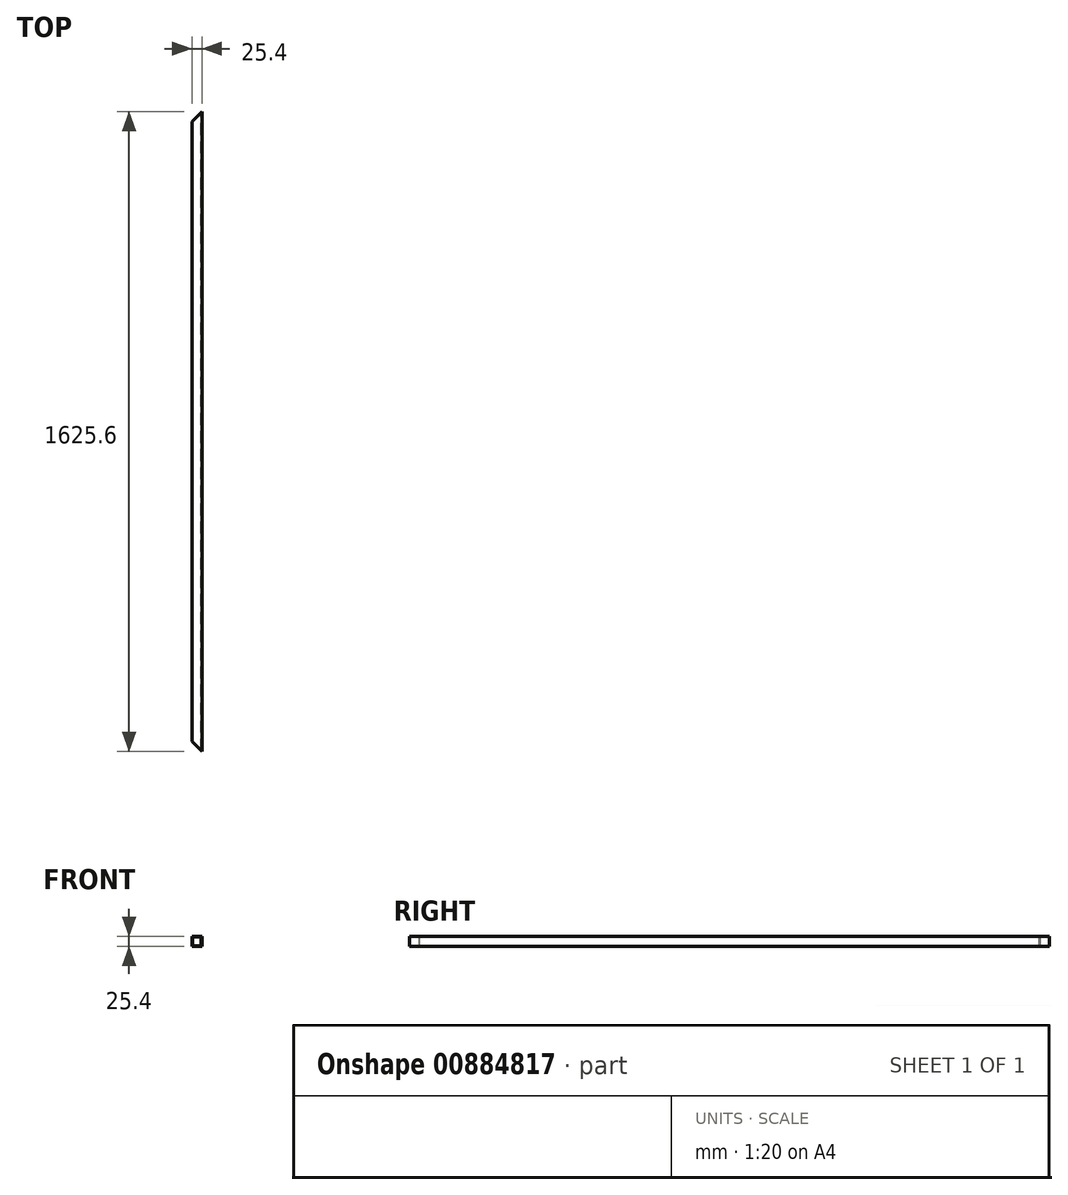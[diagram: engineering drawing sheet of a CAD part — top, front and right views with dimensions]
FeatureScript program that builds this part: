
annotation { "Feature Type Name" : "Feature", "Feature Type Description" : "" }
export const myFeature = defineFeature(function(context is Context, id is Id, definition is map)
    precondition{}
    {
        {
            var Q0;
            Q0=qCreatedBy(makeId("Front.planeOp"),FACE);
            var sketch = newSketch(context, id + "F0", { "sketchPlane" : qUnion([Q0])});
            skLineSegment(sketch, "E0.bottom", {"start": v(0, 0) * mm, "end": v(25.4, 0) * mm});
            skLineSegment(sketch, "E0.top", {"start": v(0, 25.4) * mm, "end": v(25.4, 25.4) * mm});
            skLineSegment(sketch, "E0.left", {"start": v(0, 0) * mm, "end": v(0, 25.4) * mm});
            skLineSegment(sketch, "E0.right", {"start": v(25.4, 0) * mm, "end": v(25.4, 25.4) * mm});
            skLineSegment(sketch, "E1.0", {"start": v(1.65, 1.65) * mm, "end": v(23.75, 1.65) * mm});
            skLineSegment(sketch, "E1.1", {"start": v(1.65, 1.65) * mm, "end": v(1.65, 23.75) * mm});
            skLineSegment(sketch, "E1.2", {"start": v(1.65, 23.75) * mm, "end": v(23.75, 23.75) * mm});
            skLineSegment(sketch, "E1.3", {"start": v(23.75, 1.65) * mm, "end": v(23.75, 23.75) * mm});
            skSolve(sketch);
        }
        {
            var Q0;
            Q0=makeQuery(id+"F0.imprint","IMPRINT",FACE,{"disambiguationData":[TD([[makeQuery(id+"F0.imprint","IMPRINT",EDGE,{"derivedFrom":sQuery(id+"F0.wireOp",EDGE,"E0.bottom")}),1.0]])]});
            extrude(context, id + "F1", {"entities" : qUnion([Q0]), "depth" : 1625.6 * mm, "offsetDistance" : 25.4 * mm});
        }
        {
            var Q0;
            Q0=makeQuery(id+"F1.opExtrude","SWEPT_FACE",FACE,{"disambiguationData":[OSD([sQuery(id+"F0.wireOp",EDGE,"E0.top")])]});
            var sketch = newSketch(context, id + "F2", { "sketchPlane" : qUnion([Q0])});
            skLineSegment(sketch, "E2", {"start": v(25.4, -1625.6) * mm, "end": v(0, -1600.2) * mm});
            skLineSegment(sketch, "E3", {"start": v(0, -1600.2) * mm, "end": v(0, -1625.6) * mm});
            skLineSegment(sketch, "E4", {"start": v(0, -1625.6) * mm, "end": v(25.4, -1625.6) * mm});
            skSolve(sketch);
        }
        {
            var Q0;
            Q0 = qSketchRegion(id + "F2", true);
            extrude(context, id + "F3", {"entities" : qUnion([Q0]), "operationType" : NewBodyOperationType.REMOVE, "endBound" : BoundingType.THROUGH_ALL, "oppositeDirection" : true, "depth" : 25.4 * mm, "offsetDistance" : 25.4 * mm});
        }
        {
            var Q0;
            Q0=makeQuery(id+"F1.opExtrude","SWEPT_FACE",FACE,{"disambiguationData":[OSD([sQuery(id+"F0.wireOp",EDGE,"E0.top")])]});
            var sketch = newSketch(context, id + "F4", { "sketchPlane" : qUnion([Q0])});
            skLineSegment(sketch, "E5", {"start": v(25.4, 0) * mm, "end": v(0, -25.4) * mm});
            skLineSegment(sketch, "E6", {"start": v(25.4, 0) * mm, "end": v(0, 0) * mm});
            skLineSegment(sketch, "E7", {"start": v(0, 0) * mm, "end": v(0, -25.4) * mm});
            skSolve(sketch);
        }
        {
            var Q0;
            Q0 = qSketchRegion(id + "F4", true);
            extrude(context, id + "F5", {"entities" : qUnion([Q0]), "operationType" : NewBodyOperationType.REMOVE, "endBound" : BoundingType.THROUGH_ALL, "oppositeDirection" : true, "depth" : 25.4 * mm, "offsetDistance" : 25.4 * mm});
        }
    });
